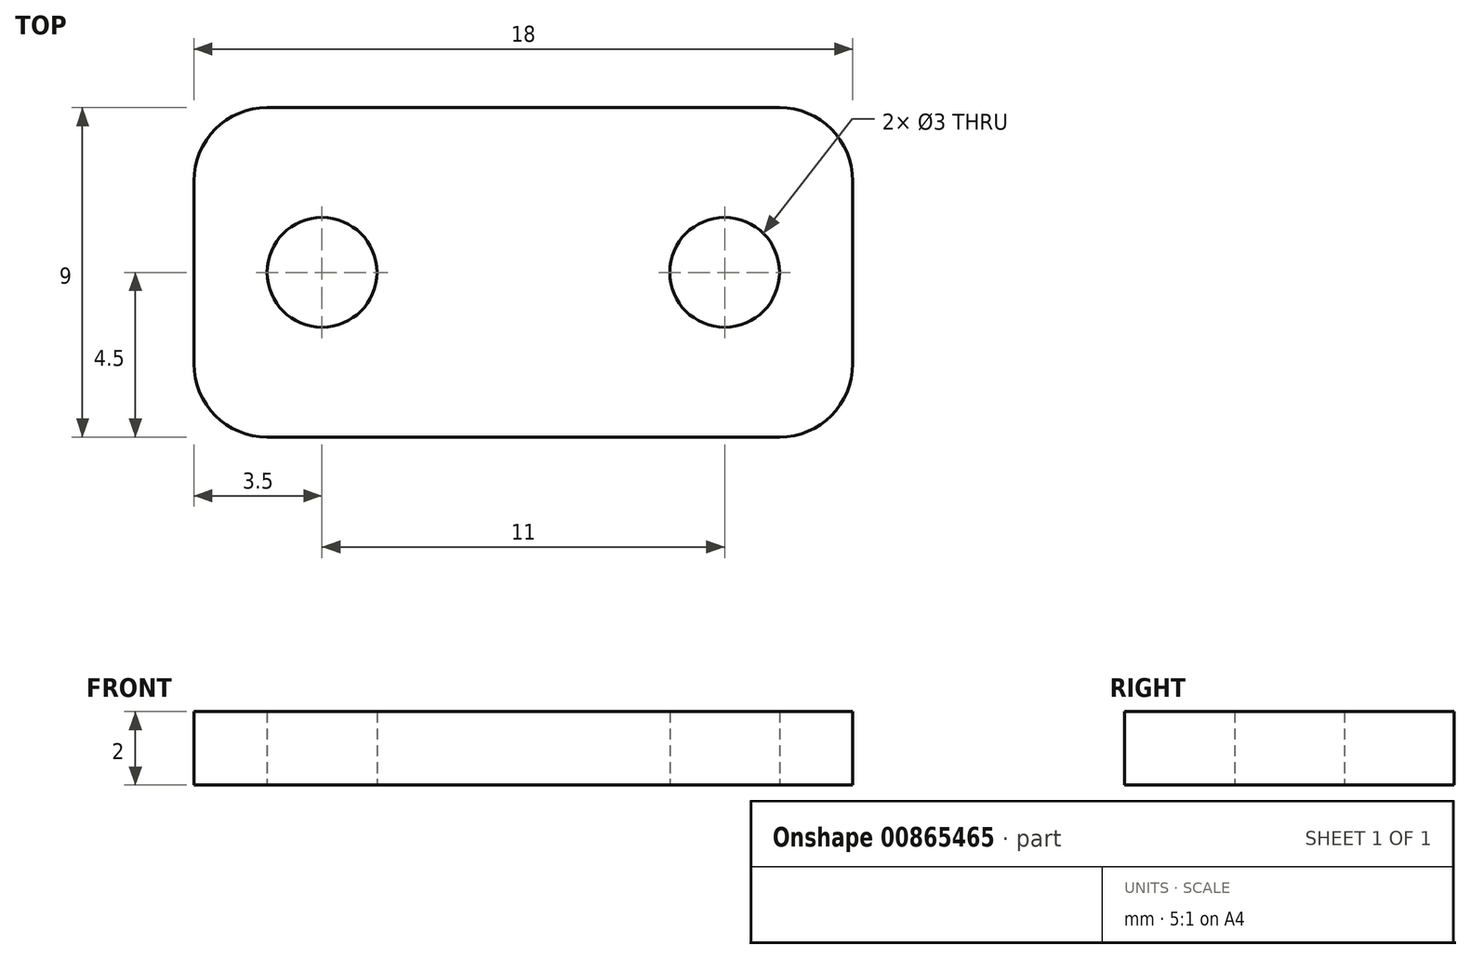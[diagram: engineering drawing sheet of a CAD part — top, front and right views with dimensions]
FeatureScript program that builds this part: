
annotation { "Feature Type Name" : "Feature", "Feature Type Description" : "" }
export const myFeature = defineFeature(function(context is Context, id is Id, definition is map)
    precondition{}
    {
        {
            var Q0;
            Q0=qCreatedBy(makeId("Top.planeOp"),FACE);
            var sketch = newSketch(context, id + "F0", { "sketchPlane" : qUnion([Q0])});
            skLineSegment(sketch, "E0.bottom", {"start": v(7, 4.5) * mm, "end": v(-7, 4.5) * mm});
            skLineSegment(sketch, "E0.top", {"start": v(7, -4.5) * mm, "end": v(-7, -4.5) * mm});
            skLineSegment(sketch, "E0.left", {"start": v(9, 2.5) * mm, "end": v(9, -2.5) * mm});
            skLineSegment(sketch, "E0.right", {"start": v(-9, 2.5) * mm, "end": v(-9, -2.5) * mm});
            skPoint(sketch, "E0.middle", {"position": v(0, 0) * mm});
            skCircle(sketch, "E1", {"center": v(-5.5, 0) * mm, "radius": 1.5 * mm});
            skCircle(sketch, "E2", {"center": v(5.5, 0) * mm, "radius": 1.5 * mm});
            skPoint(sketch, "E3.visualSharp", {"position": v(-9, 4.5) * mm});
            skArc(sketch, "E3.filletArc", {"start": v(-7, 4.5) * mm, "mid": v(-8.41, 3.91) * mm, "end": v(-9, 2.5) * mm});
            skPoint(sketch, "E4.visualSharp", {"position": v(-9, -4.5) * mm});
            skArc(sketch, "E4.filletArc", {"start": v(-9, -2.5) * mm, "mid": v(-8.41, -3.91) * mm, "end": v(-7, -4.5) * mm});
            skPoint(sketch, "E5.visualSharp", {"position": v(9, -4.5) * mm});
            skArc(sketch, "E5.filletArc", {"start": v(7, -4.5) * mm, "mid": v(8.41, -3.91) * mm, "end": v(9, -2.5) * mm});
            skPoint(sketch, "E6.visualSharp", {"position": v(9, 4.5) * mm});
            skArc(sketch, "E6.filletArc", {"start": v(9, 2.5) * mm, "mid": v(8.41, 3.91) * mm, "end": v(7, 4.5) * mm});
            skSolve(sketch);
        }
        {
            var Q0;
            Q0 = qSketchRegion(id + "F0", true);
            extrude(context, id + "F1", {"entities" : qUnion([Q0]), "depth" : 2 * mm, "offsetDistance" : 25 * mm});
        }
    });
